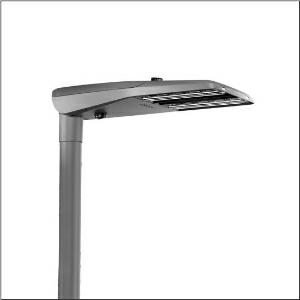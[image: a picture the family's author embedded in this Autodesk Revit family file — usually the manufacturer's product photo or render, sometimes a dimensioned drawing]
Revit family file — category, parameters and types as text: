
# Revit family: streetlight_sl_11_iq_midi___st1_2a_5xc3a41y08le_52ec
name_source: partatom
category: Lighting Fixtures
units: mm (PartAtom-declared; Revit-internal decimal feet)

## family parameters
Cut with Voids When Loaded = No
Host = Face
Light Source = No
Part Type = Normal
Room Calculation Point = No
Round Connector Dimension = Use Diameter
Shared = No

## types (1)
- --- (1 x LED, 9590 lm, 59.4 W, 4000K)
    Apparent Load = 59 VA
    CIE Flux Codes = 32 70 96 100 100
    Color Rendering = 70
    Color Temperature = 4000K
    Default Elevation = 1800 mm
    Description = Streetlight SL 11 iQ midi, mast luminaire, primary light control with 3 zone facetted reflector, of plastic, silver coated, highly specular, primary optical cover: cover, of PMMA, transparent, light distribution: ST1.2a, light emission: direct distribution, primary light characteristic: asymmetric, installation type: post-top, side-entry, lamps: LED, High Power LED, rated values: 9.590lm | 59,4W | 161,4lm/W (begin service life); end service life: 9.590lm | 61,6W; at 50% lumin. flux: 4.795lm | 28,5W | 168,2lm/W, colour temperature: 4000K, colour rendering: CRI > 70, light colour: 740, light setting 1 begin service life: 100% | 9.590lm | 59,4W | 161,4lm/W | 4.000K, light setting 1 end service life: 61,6W, further light settings possible, control: pre-setting: logarithmic dimming characteristic, Street-Remote, Auto-Match, Temp-Guard, Lumen-Switch, Night-Set, Smart-Wire, Light-Fading, Desk-Remote (wireless, voltage-free reading and setting of iQ features in the workshop via application-optimized NFC function/RFID function), optimised constant luminous flux control (CLO 2.0), with cable H07RN-F 3x 1.5mm², mains connection: 230..240V, AC, 50/60Hz, connection cable pre-assembled, cable length: 8,5m, luminaire housing, of diecast aluminium, powder-coated, SITECO metallic grey (DB 702S), please order mast flange separately, inclination adjustable without tools: 0°, 5°, 10°, 15° (post-top) | 0°, -5°, -10°, -15° (side-entry), sealing non-destructively replaceable, multi-level sealing system, length: 780mm, width: 376mm, height: 118mm, mast flange for spigot size: 42mm (side-entry): 5XC10008XM4, 60/48mm (side-entry/post-top): 5XC10108XM2, 76/60mm (side-entry/post-top): 5XC10108XM1, equipment: standard, Smart Interface below and above, protection rating (complete): IP66, insulation class (complete): insulation class II (safety insulation), certification: CE, ENEC, ENEC+, VDE, UKCA, impact resistance: IK10, permissible operating ambient temperature for outdoor applications: -25..+50°C, standard-compliant lighting for roads and squares, Environmental Product Declaration (EPD) tested and certified by an independent institute, packaging unit: 1 piece

Light Distribution: ST1.2a
    Height = 118 mm
    Lamp = 1 x LED
    Lamp Light Flux = 9590 lm
    Lamp Power = 59.4 W
    Lamp count = 1
    Length = 780 mm
    Luminous efficacy = 161 lm/W
    Manufacturer = Siteco
    ModVariant = No
    Model = 5XC3A41Y08LE
    Number of Poles = 1
    OnlyDefault = Yes
    Power Factor = 1
    Product Name = Streetlight SL 11 iQ midi | ST1.2a
    Product group = mast luminaire | pylon top
    ProductGroupID = 6100
    Protection Class = Protection class II
    Protection Degree = IP 66
    RLX_Detail_Level = 1
    RLX_Emergency_Light_Flux = 0 lm
    RLX_Emergency_Type = 0
    RLX_Emergency_Type_DB = No
    RlxData = <blob elided: 69897 chars, md5=cd3472a2>
    Socket = socket
    Standby Power = 0 W
    System Light Flux = 9590 lm
    System Power = 59 W
    Type Comments = factory setting: luminous flux: 100 % | dim-lin: 254 | 521 mA
    Type Image = l_1004429.jpg
    URL = http://relux.com
    VarID = @adj_132727
    Voltage = 0 V
    Weight = 0.00 kg
    Width = 376 mm

## geometry (parser evidence)
native form markers: Blend x4, Sweep x10
no freeform markers — native parametric forms only
